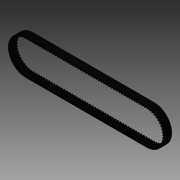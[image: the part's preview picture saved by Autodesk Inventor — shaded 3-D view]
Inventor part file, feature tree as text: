
AUTODESK INVENTOR PART (.ipt)
format: ipt  version: 2014 SP1 (Build 180222100, 222)  size: 1,107,968 bytes
history: native  units: mm
features: extrude x2, sketch x2, pattern_linear x1
ambient origin geometry x8: Origin, YZ Plane, XZ Plane, XY Plane, X Axis, Y Axis, Z Axis, Center Point
bodies: Solid1 (feature_tree)
feature tree (5):
  extrude  "Extrusion1"  Depth=15.0mm
  sketch  "Sketch2"  dims[d3=0.416667mm d4=1.5625mm d5=1.73mm d6=0.520833mm d7=0.100833mm d8=33.8201mm d10=235.747492mm d12=1370.0mm d15=607.801mm d16=65.532mm d19=15.0mm d20=0.0mm d22=0.25mm d23=1.73mm]
  pattern_linear  "Rectangular Pattern1"  Spacing1=1.5625mm  [1 undecoded]
  extrude  "Extrusion2"  Depth=1.73mm
  sketch  "Sketch1"  dims[d0=15.0mm d1=0.0mm d2=5.0mm]
note: 1 required parameter value undecoded (feature->parameter linkage not recoverable at this tier; creation-order binding heuristic only, values carry confidence <= 0.55)
